# Revit family: Hekatron_Feststellanlagen_DKT 01 gr_DE_22.01
name_source: partatom
category: Brandmelder
revit_build: Autodesk Revit 2018 (Build: 20190510_1515(x64)
units: mm (PartAtom-declared; Revit-internal decimal feet)

## family parameters
Basisbauteil = Fläche
Beim Laden mit Abzugskörper schneiden = Nein
Bemaßung runder Anschluss = Durchmesser verwenden
Beschriftungsausrichtung beibehalten = Ja
Gemeinsam genutzt = Nein
OmniClass-Nummer = 23.85.30.21
OmniClass-Titel = Environmental Detection/Registration
Raumberechnungspunkt = Nein
Teiletyp = Normal

## types (1)
- DKT 01 gr
    Beschreibung = Aufputz, als Handauslöser für Feststellanlage maschinellen Rauchabzugsanlagen
    Betriebsspannung = 24 V DC
    Breite (mm) = 31.0
    Farbe = grau, ähnlich RAL 7023
    Hersteller = Hekatron
    Höhe (mm) = 130.0
    Kabeleinführung = oben, unten, hinten
    Link zu Produktinformation = https://www.hekatron-planungstools.de
    Link zu ausschreiben.de = http://www.ausschreiben.de
    Material = Polycarbonat
    Modell = DKT 01 gr
    Montageart = Aufputz
    Schutzart = IP 20
    Stromaufnahme = 10mA
    Tiefe (mm) = 130.0
    Typenkommentare = Druckknopftaster DKT 01 grau
    UB A&S Artikel Nummer = 6200115
    URL = www.hekatron-brandschutz.de
    Version des BIM Objektes = 22.01
    Vorgabe-Ansicht = 1200 mm

## geometry (parser evidence)
native form markers: Sweep x2
no freeform markers — native parametric forms only
